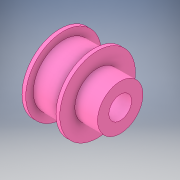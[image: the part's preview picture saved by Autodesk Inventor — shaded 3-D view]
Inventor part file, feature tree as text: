
AUTODESK INVENTOR PART (.ipt)
format: ipt  version: 2017 SP1 (Build 210196100, 196)  size: 138,752 bytes
history: native  units: in
note: dims shown in document units (in); Inventor stores cm internally (conversion verified against a paired STEP export)
features: extrude x4, sketch x4
ambient origin geometry x8: Origin, YZ Plane, XZ Plane, XY Plane, X Axis, Y Axis, Z Axis, Center Point
bodies: Solid1 (feature_tree)
feature tree (8):
  extrude  "Extrusion1"  Depth=0.375in
  extrude  "Extrusion2"  Depth=0.5in
  extrude  "Extrusion3"  Depth=0.0625in TaperAngle=0.0deg
  extrude  "Extrusion4"  Depth=0.375in TaperAngle=0.0deg
  sketch  "Sketch1"  dims[d0=1.0in d2=0.375in]
  sketch  "Sketch2"  dims[d4=0.5in d5=0.0in d6=0.125in]
  sketch  "Sketch3"  dims[d7=0.0625in d8=0.0in d9=0.0625in d10=0.0in]
  sketch  "Sketch4"  dims[d11=0.1875in d12=0.375in d13=0.0in]
